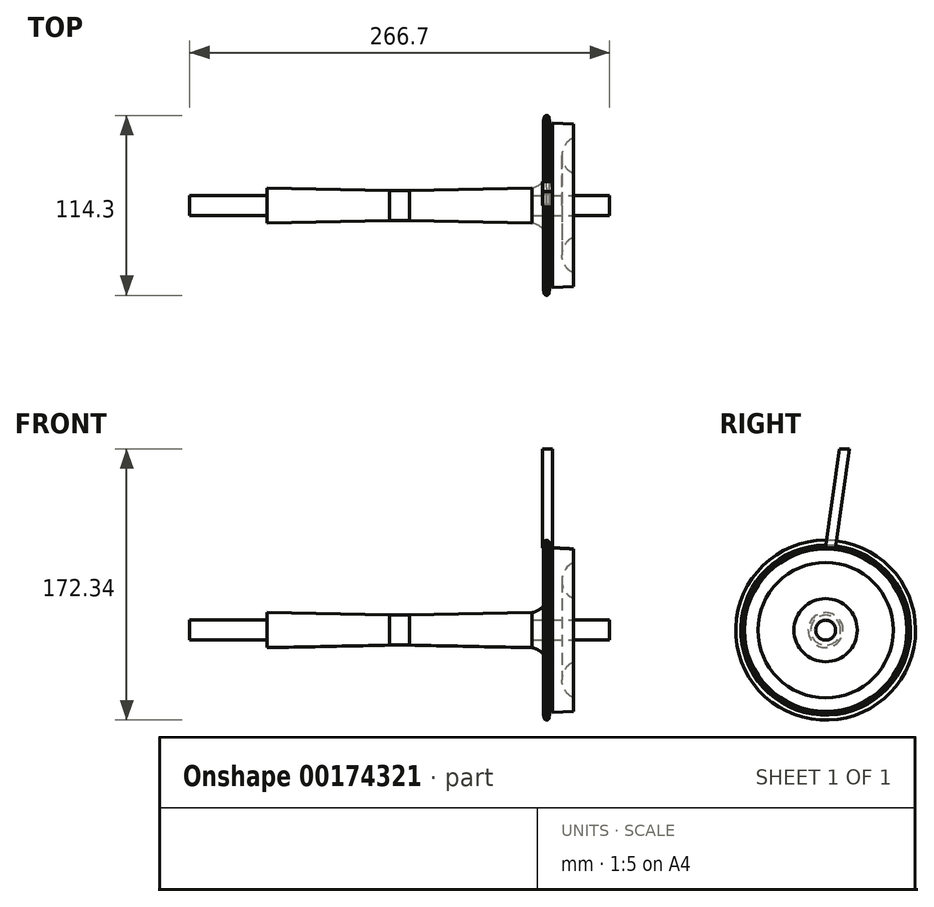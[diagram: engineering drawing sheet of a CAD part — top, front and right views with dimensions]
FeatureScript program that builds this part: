
annotation { "Feature Type Name" : "Feature", "Feature Type Description" : "" }
export const myFeature = defineFeature(function(context is Context, id is Id, definition is map)
    precondition{}
    {
        {
            var Q0;
            Q0=qCreatedBy(makeId("Front.planeOp"),FACE);
            var sketch = newSketch(context, id + "F0", { "sketchPlane" : qUnion([Q0])});
            skLineSegment(sketch, "E0", {"start": v(0, 23.93) * mm, "end": v(0, 0) * mm});
            skLineSegment(sketch, "E1", {"start": v(0, 0) * mm, "end": v(133.35, 0) * mm});
            skLineSegment(sketch, "E2.0", {"start": v(0, 9.53) * mm, "end": v(6.35, 9.53) * mm});
            skLineSegment(sketch, "E3.0", {"start": v(84.14, 23.93) * mm, "end": v(84.14, 6.35) * mm});
            skLineSegment(sketch, "E4", {"start": v(6.35, 9.53) * mm, "end": v(84.14, 11.11) * mm});
            skLineSegment(sketch, "E5.0", {"start": v(133.35, 23.93) * mm, "end": v(133.35, 0) * mm});
            skLineSegment(sketch, "E6.0", {"start": v(84.14, 6.35) * mm, "end": v(133.35, 6.35) * mm});
            skPoint(sketch, "E7.orphan", {"position": v(84.14, 0) * mm});
            skPoint(sketch, "E8.orphan", {"position": v(9.53, 0) * mm});
            skLineSegment(sketch, "E9.MirrorCS", {"start": v(0, 9.53) * mm, "end": v(-6.35, 9.53) * mm});
            skLineSegment(sketch, "E10.MirrorCS", {"start": v(-6.35, 9.53) * mm, "end": v(-84.14, 11.11) * mm});
            skLineSegment(sketch, "E11.MirrorCS", {"start": v(-84.14, 23.93) * mm, "end": v(-84.14, 6.35) * mm});
            skLineSegment(sketch, "E12.MirrorCS", {"start": v(-84.14, 6.35) * mm, "end": v(-133.35, 6.35) * mm});
            skLineSegment(sketch, "E13.MirrorCS", {"start": v(-133.35, 23.93) * mm, "end": v(-133.35, 0) * mm});
            skLineSegment(sketch, "E14.MirrorCS", {"start": v(0, 0) * mm, "end": v(-133.35, 0) * mm});
            skSolve(sketch);
        }
        {
            var Q0;
            {var subQ3=sQuery(id+"F0.wireOp",EDGE,"E9.MirrorCS");Q0=makeQuery(id+"F0.imprint","IMPRINT",FACE,{"disambiguationData":[TD([[makeQuery(id+"F0.imprint","IMPRINT",EDGE,{"derivedFrom":subQ3}),1.0]])]});}
            var Q1;
            {var subQ4=sQuery(id+"F0.wireOp",EDGE,"E1");Q1=makeQuery(id+"F0.imprint","IMPRINT",FACE,{"disambiguationData":[TD([[makeQuery(id+"F0.imprint","IMPRINT",EDGE,{"derivedFrom":subQ4}),1.0]])]});}
            var Q2;
            Q2=sQuery(id+"F0.wireOp",EDGE,"E14.MirrorCS");
            revolve(context, id + "F1", {"entities" : qUnion([Q0, Q1]), "axis" : qUnion([Q2]), "revolveType" : RevolveType.FULL});
        }
        {
            var Q0;
            Q0=qCreatedBy(makeId("Front.planeOp"),FACE);
            var sketch = newSketch(context, id + "F2", { "sketchPlane" : qUnion([Q0])});
            skLineSegment(sketch, "E15.0", {"start": v(84.14, 11.11) * mm, "end": v(84.14, -11.11) * mm});
            skLineSegment(sketch, "E16.0", {"start": v(91.28, 53.42) * mm, "end": v(91.28, 35.06) * mm});
            skLineSegment(sketch, "E17", {"start": v(93.26, 57.15) * mm, "end": v(95.24, 57.15) * mm, "construction": true});
            skLineSegment(sketch, "E18.0", {"start": v(110.33, 51.6) * mm, "end": v(110.33, 43) * mm});
            skLineSegment(sketch, "E19", {"start": v(84.14, 11.11) * mm, "end": v(159.6, 11.11) * mm, "construction": true});
            skLineSegment(sketch, "E20.0", {"start": v(95.24, 53.69) * mm, "end": v(95.24, 52.4) * mm});
            skLineSegment(sketch, "E21.0", {"start": v(91.28, 52.4) * mm, "end": v(95.24, 52.4) * mm, "construction": true});
            skLineSegment(sketch, "E22", {"start": v(96.93, 52.31) * mm, "end": v(110.33, 51.6) * mm});
            skLineSegment(sketch, "E23", {"start": v(82.74, 0) * mm, "end": v(84.14, 0) * mm, "construction": true});
            skLineSegment(sketch, "E24.0", {"start": v(91.28, 53.42) * mm, "end": v(95.24, 53.42) * mm, "construction": true});
            skLineSegment(sketch, "E25", {"start": v(91.28, 53.42) * mm, "end": v(91.71, 55.86) * mm});
            skLineSegment(sketch, "E26", {"start": v(93.26, 55.37) * mm, "end": v(93.26, 58.28) * mm, "construction": true});
            skPoint(sketch, "E27.orphan", {"position": v(95.24, 53.42) * mm});
            skArc(sketch, "E28", {"start": v(93.26, 57.15) * mm, "mid": v(92.23, 56.69) * mm, "end": v(91.68, 55.7) * mm});
            skArc(sketch, "E29.MirrorCS", {"start": v(93.26, 57.15) * mm, "mid": v(94.3, 56.69) * mm, "end": v(94.84, 55.7) * mm});
            skLineSegment(sketch, "E30.MirrorCS", {"start": v(95.24, 53.42) * mm, "end": v(95.24, 53.42) * mm});
            skArc(sketch, "E31", {"start": v(95.16, 53.92) * mm, "mid": v(95.83, 52.88) * mm, "end": v(96.93, 52.31) * mm});
            skLineSegment(sketch, "E32.trimOffspring", {"start": v(95.16, 53.92) * mm, "end": v(94.81, 55.86) * mm});
            skLineSegment(sketch, "E33.trimOffspring", {"start": v(84.14, 0) * mm, "end": v(110.33, 0) * mm, "construction": true});
            skLineSegment(sketch, "E34", {"start": v(91.28, 0) * mm, "end": v(110.33, 0) * mm});
            skArc(sketch, "E35", {"start": v(84.14, 11.11) * mm, "mid": v(94.49, 20.72) * mm, "end": v(91.48, 34.53) * mm});
            skPoint(sketch, "E36.visualSharp", {"position": v(91.28, 34.75) * mm});
            skArc(sketch, "E36.filletArc", {"start": v(91.28, 35.06) * mm, "mid": v(91.33, 34.77) * mm, "end": v(91.48, 34.53) * mm});
            skLineSegment(sketch, "E37", {"start": v(110.33, 0) * mm, "end": v(84.14, 0) * mm});
            skArc(sketch, "E38", {"start": v(110.33, 43) * mm, "mid": v(103.02, 31.54) * mm, "end": v(110.33, 20.08) * mm});
            skLineSegment(sketch, "E39.trimOffspring", {"start": v(110.33, 20.08) * mm, "end": v(110.33, 0) * mm});
            skSolve(sketch);
        }
        {
            var Q0;
            Q0 = qSketchRegion(id + "F2", true);
            var Q1;
            Q1=sQuery(id+"F2.wireOp",EDGE,"E34");
            revolve(context, id + "F3", {"entities" : qUnion([Q0]), "axis" : qUnion([Q1]), "revolveType" : RevolveType.FULL});
        }
        {
            var Q0;
            Q0=qCreatedBy(makeId("Right.planeOp"),FACE);
            var sketch = newSketch(context, id + "F4", { "sketchPlane" : qUnion([Q0])});
            skCircle(sketch, "E40.0", {"center": v(0, 0) * mm, "radius": 57.15 * mm, "construction": true});
            skLineSegment(sketch, "E41", {"start": v(0, 57.15) * mm, "end": v(6.29, 58.03) * mm});
            skLineSegment(sketch, "E42", {"start": v(6.29, 58.03) * mm, "end": v(4.62, 69.93) * mm});
            skSolve(sketch);
        }
        {
            var Q0;
            Q0=qCreatedBy(makeId("Front.planeOp"),FACE);
            var sketch = newSketch(context, id + "F5", { "sketchPlane" : qUnion([Q0])});
            skLineSegment(sketch, "E43", {"start": v(91.28, 53.42) * mm, "end": v(91.68, 55.7) * mm});
            skArc(sketch, "E44", {"start": v(93.26, 57.15) * mm, "mid": v(92.23, 56.69) * mm, "end": v(91.68, 55.7) * mm});
            skArc(sketch, "E45", {"start": v(94.84, 55.7) * mm, "mid": v(94.3, 56.69) * mm, "end": v(93.26, 57.15) * mm});
            skLineSegment(sketch, "E46", {"start": v(94.84, 55.7) * mm, "end": v(95.16, 53.92) * mm});
            skArc(sketch, "E47", {"start": v(95.16, 53.92) * mm, "mid": v(95.83, 52.88) * mm, "end": v(96.93, 52.31) * mm});
            skLineSegment(sketch, "E48.0", {"start": v(96.93, -52.31) * mm, "end": v(96.93, 52.31) * mm});
            skLineSegment(sketch, "E49.0", {"start": v(91.28, -53.42) * mm, "end": v(91.28, 53.42) * mm});
            skPoint(sketch, "E50", {"position": v(91.28, 53.42) * mm});
            skLineSegment(sketch, "E51", {"start": v(91.28, 53.42) * mm, "end": v(91.28, 58) * mm, "construction": true});
            skLineSegment(sketch, "E52.0", {"start": v(90.6, 52.31) * mm, "end": v(90.6, 115.81) * mm});
            skLineSegment(sketch, "E53", {"start": v(96.93, 52.31) * mm, "end": v(88.91, 52.31) * mm});
            skLineSegment(sketch, "E54", {"start": v(96.93, 52.31) * mm, "end": v(96.93, 115.81) * mm});
            skLineSegment(sketch, "E55", {"start": v(96.93, 115.81) * mm, "end": v(90.58, 115.81) * mm});
            skSolve(sketch);
        }
        {
            var Q0;
            {var subQ1=sQuery(id+"F5.wireOp",EDGE,"E43");Q0=makeQuery(id+"F5.imprint","IMPRINT",FACE,{"disambiguationData":[TD([[makeQuery(id+"F5.imprint","IMPRINT",EDGE,{"derivedFrom":subQ1}),1.0]])]});}
            var Q1;
            Q1=sQuery(id+"F4.wireOp",EDGE,"E41");
            sweep(context, id + "F6", {"profiles" : qUnion([Q0]), "path" : qUnion([Q1])});
        }
        {
            var Q0;
            Q0=makeQuery(id+"F6.opSweep","SWEPT_BODY",BODY,{"disambiguationData":[OSD([sQuery(id+"F4.wireOp",EDGE,"E41"),sQuery(id+"F5.wireOp",EDGE,"E43"),sQuery(id+"F5.wireOp",EDGE,"E44"),sQuery(id+"F5.wireOp",EDGE,"E45"),sQuery(id+"F5.wireOp",EDGE,"E46"),sQuery(id+"F5.wireOp",EDGE,"E47"),sQuery(id+"F5.wireOp",EDGE,"E49.0"),sQuery(id+"F5.wireOp",EDGE,"E52.0"),sQuery(id+"F5.wireOp",EDGE,"E53"),sQuery(id+"F5.wireOp",EDGE,"E54"),sQuery(id+"F5.wireOp",EDGE,"E55")])]});
            var Q1;
            Q1=sQuery(id+"F2.wireOp",EDGE,"E21.0");
            transform(context, id + "F7", {"entities" : qUnion([Q0]), "transformType" : TransformType.ROTATION, "transformAxis" : qUnion([Q1]), "angle" : 352 * degree, "makeCopy" : false});
        }
    });
